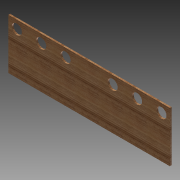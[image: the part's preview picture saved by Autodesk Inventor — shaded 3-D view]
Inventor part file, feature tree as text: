
AUTODESK INVENTOR PART (.ipt)
format: ipt  version: 2012 (Build 160160000, 160)  size: 103,424 bytes
history: native  units: in
note: dims shown in document units (in); Inventor stores cm internally (conversion verified against a paired STEP export)
features: extrude x1, sketch x1
ambient origin geometry x8: Origin, YZ Plane, XZ Plane, XY Plane, X Axis, Y Axis, Z Axis, Center Point
bodies: Solid1 (feature_tree)
feature tree (2):
  extrude  "Extrusion1"  Depth=24.0in
  sketch  "Sketch1"  dims[d0=7.5in d1=24.0in d11=0.25in d12=0.0in d13=1.5in d14=1.5in d15=7.0in d16=7.25in d17=3.625in d18=3.625in d19=1.25in d20=23.5in d21=1.25in d22=1.25in d23=1.25in]
